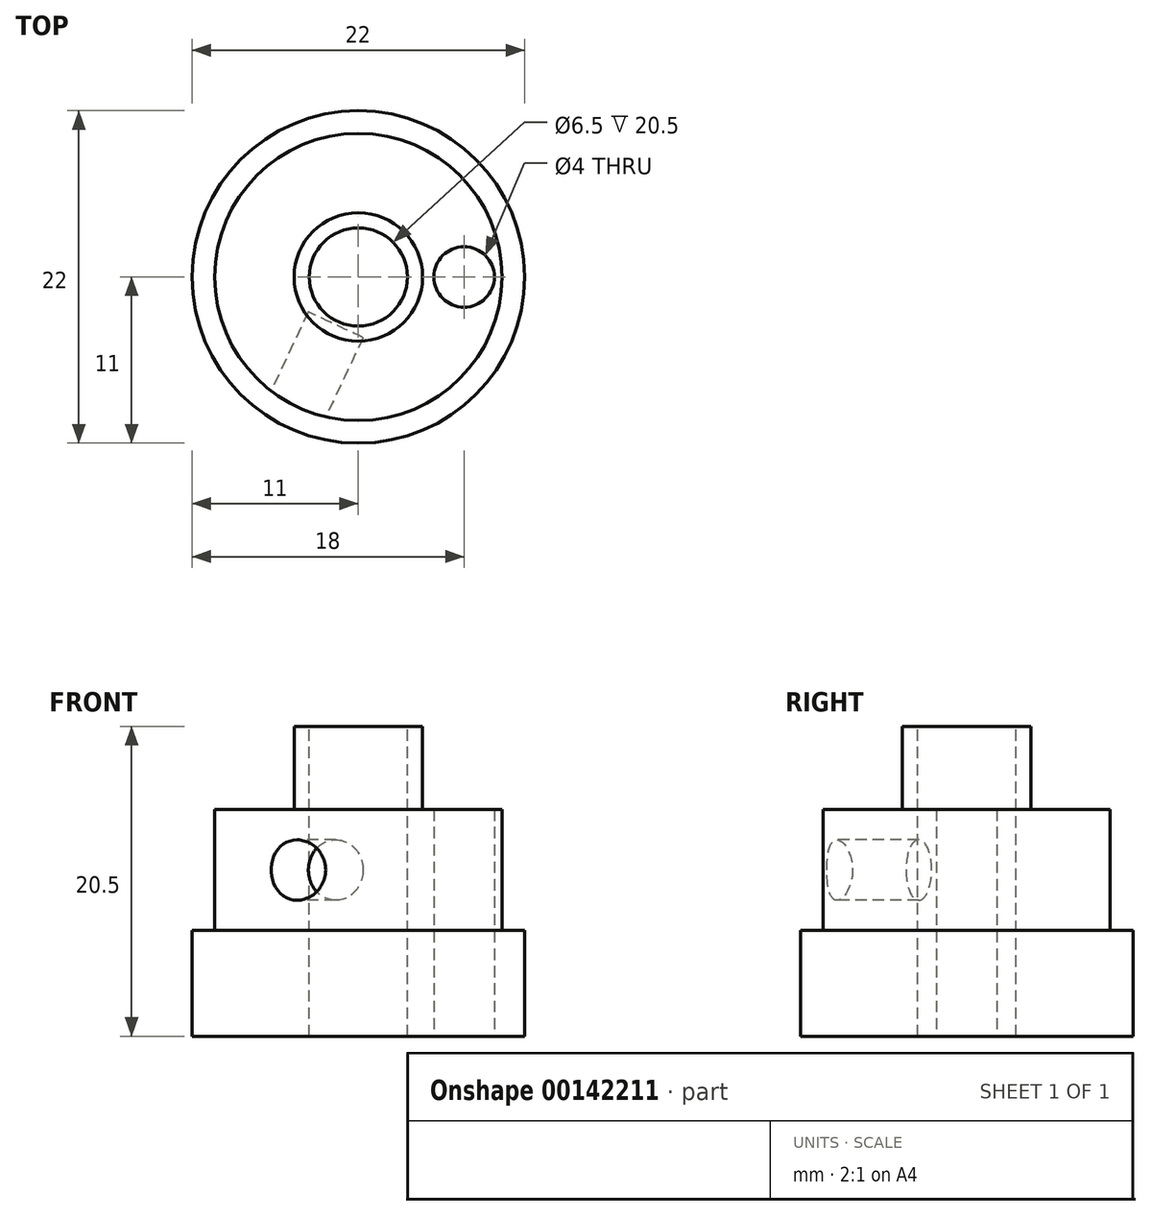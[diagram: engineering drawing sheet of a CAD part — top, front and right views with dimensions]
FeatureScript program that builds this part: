
annotation { "Feature Type Name" : "Feature", "Feature Type Description" : "" }
export const myFeature = defineFeature(function(context is Context, id is Id, definition is map)
    precondition{}
    {
        {
            var Q0;
            Q0=qCreatedBy(makeId("Top.planeOp"),FACE);
            var sketch = newSketch(context, id + "F0", { "sketchPlane" : qUnion([Q0])});
            skCircle(sketch, "E0", {"center": v(0, 0) * mm, "radius": 11 * mm});
            skSolve(sketch);
        }
        {
            var Q0;
            Q0=qSketchRegion(id+"F0",true);
            extrude(context, id + "F1", {"entities" : qUnion([Q0]), "depth" : 7 * mm});
        }
        {
            var Q0;
            Q0=makeQuery(id+"F1.opExtrude","CAP_FACE",FACE,{"disambiguationData":[OSD([sQuery(id+"F0.wireOp",EDGE,"E0")])],"isStart":false});
            var sketch = newSketch(context, id + "F2", { "sketchPlane" : qUnion([Q0])});
            skCircle(sketch, "E1", {"center": v(0, 0) * mm, "radius": 9.5 * mm});
            skSolve(sketch);
        }
        {
            var Q0;
            Q0=qSketchRegion(id+"F2",true);
            var Q1;
            Q1=qSketchRegion(id+"F4",true);
            extrude(context, id + "F3", {"entities" : qUnion([Q0, Q1]), "operationType" : NewBodyOperationType.ADD, "depth" : 8 * mm});
        }
        {
            var Q0;
            Q0=makeQuery(id+"F3.opExtrude","CAP_FACE",FACE,{"disambiguationData":[OSD([sQuery(id+"F2.wireOp",EDGE,"E1")])],"isStart":false});
            var sketch = newSketch(context, id + "F4", { "sketchPlane" : qUnion([Q0])});
            skCircle(sketch, "E2", {"center": v(0, 0) * mm, "radius": 4.25 * mm});
            skSolve(sketch);
        }
        {
            var Q0;
            Q0=qSketchRegion(id+"F4",true);
            extrude(context, id + "F5", {"entities" : qUnion([Q0]), "operationType" : NewBodyOperationType.ADD, "depth" : 5.5 * mm});
        }
        {
            var Q0;
            Q0=makeQuery(id+"F5.opExtrude","CAP_FACE",FACE,{"disambiguationData":[OSD([sQuery(id+"F4.wireOp",EDGE,"E2")])],"isStart":false});
            var sketch = newSketch(context, id + "F6", { "sketchPlane" : qUnion([Q0])});
            skCircle(sketch, "E3", {"center": v(0, 0) * mm, "radius": 3.25 * mm});
            skSolve(sketch);
        }
        {
            var Q0;
            Q0=makeQuery(id+"F6.imprint","IMPRINT",FACE,{"disambiguationData":[TD([[makeQuery(id+"F6.imprint","IMPRINT",EDGE,{"derivedFrom":sQuery(id+"F6.wireOp",EDGE,"E3")}),1.0]])]});
            extrude(context, id + "F7", {"entities" : qUnion([Q0]), "operationType" : NewBodyOperationType.REMOVE, "endBound" : BoundingType.THROUGH_ALL, "oppositeDirection" : true, "depth" : 25 * mm});
        }
        {
            var Q0;
            Q0=makeQuery(id+"F1.opExtrude","CAP_FACE",FACE,{"disambiguationData":[OSD([sQuery(id+"F0.wireOp",EDGE,"E0")])],"isStart":true});
            var sketch = newSketch(context, id + "F8", { "sketchPlane" : qUnion([Q0])});
            skCircle(sketch, "E4", {"center": v(7, 0) * mm, "radius": 2 * mm});
            skSolve(sketch);
        }
        {
            var Q0;
            Q0=qSketchRegion(id+"F8",true);
            extrude(context, id + "F9", {"entities" : qUnion([Q0]), "operationType" : NewBodyOperationType.REMOVE, "endBound" : BoundingType.THROUGH_ALL, "oppositeDirection" : true, "depth" : 25 * mm});
        }
        {
            var Q0;
            Q0=makeQuery(id+"F3.opExtrude","CAP_FACE",FACE,{"disambiguationData":[OSD([sQuery(id+"F2.wireOp",EDGE,"E1")])],"isStart":false});
            var sketch = newSketch(context, id + "F10", { "sketchPlane" : qUnion([Q0])});
            skCircle(sketch, "E5.0", {"center": v(7, 0) * mm, "radius": 2 * mm});
            skLineSegment(sketch, "E6", {"start": v(7, 0) * mm, "end": v(-4.05, -8.6) * mm, "construction": true});
            skLineSegment(sketch, "E7", {"start": v(-6.2, -7.57) * mm, "end": v(-1.9, -9.6) * mm, "construction": true});
            skSolve(sketch);
        }
        {
            var Q0;
            Q0=sQuery(id+"F10.wireOp",EDGE,"E7");
            cPlane(context, id + "F11", {"entities" : qUnion([Q0]), "cplaneType" : CPlaneType.LINE_ANGLE, "offset" : 25 * mm, "angle" : 0 * degree, "width" : 150 * mm, "height" : 150 * mm});
        }
        {
            var Q0;
            Q0=qCreatedBy(id+"F11.planeOp",FACE);
            var sketch = newSketch(context, id + "F12", { "sketchPlane" : qUnion([Q0])});
            skPoint(sketch, "E8.0", {"position": v(0, 15) * mm});
            skCircle(sketch, "E9", {"center": v(0, 11) * mm, "radius": 2 * mm});
            skSolve(sketch);
        }
        {
            var Q0;
            Q0=qSketchRegion(id+"F12",true);
            extrude(context, id + "F13", {"entities" : qUnion([Q0]), "operationType" : NewBodyOperationType.REMOVE, "depth" : 6 * mm});
        }
    });
